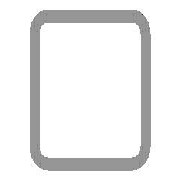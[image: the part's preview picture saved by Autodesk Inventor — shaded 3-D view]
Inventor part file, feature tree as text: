
AUTODESK INVENTOR PART (.ipt)
format: ipt  version: 2025.3 (Build 293356030, 356C)  size: 134,144 bytes
history: native  units: mm (DEFAULTED — no unit token found)
features: other x4, sketch x1, plane x1
ambient origin geometry x8: Origin, YZ Plane, XZ Plane, XY Plane, X Axis, Y Axis, Z Axis, Center Point
bodies: Solid1 (feature_tree), Body (feature_tree)
feature tree (6):
  parser-record x1  (decoder bookkeeping rows leaked as tree rows — omitted from the tree; the rows remain in map.json)
  other  "Driven Length"
  other  "Start Plane"
  other  "End Plane"
  sketch  "Sketch3"  dims[d3=2220.360331mm d4=0.0mm d7=6.0mm d9=100.0mm d11=100.0mm d12=3.0mm d13=-0.0mm d14=2220.360331mm d15=50.0mm d16=50.0mm d17=90.0deg d18=2220.360331mm]
  plane  "Work Plane3"
